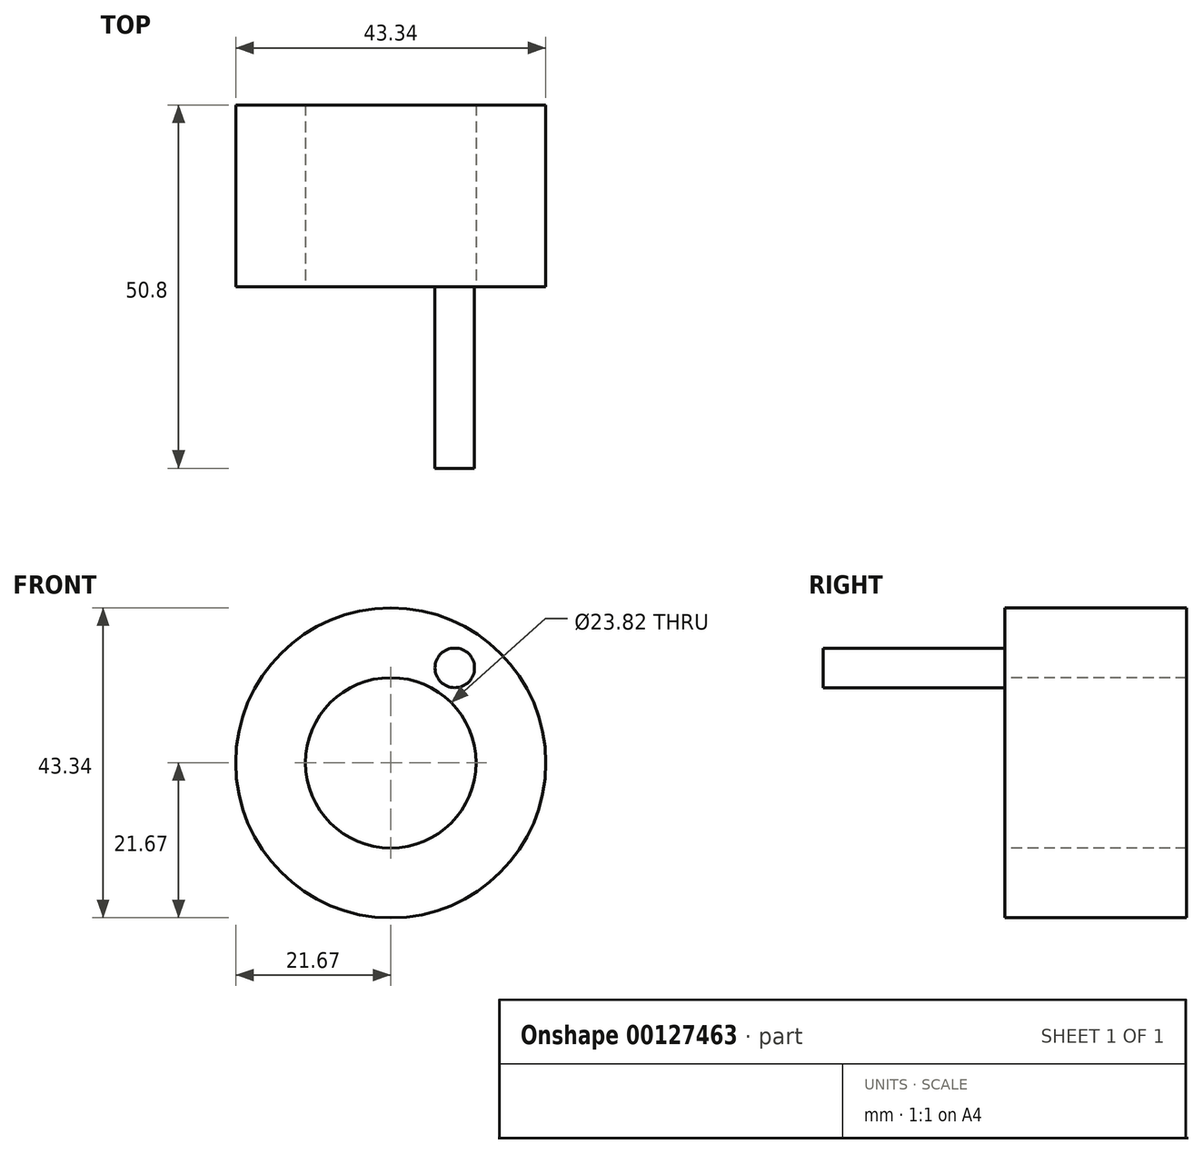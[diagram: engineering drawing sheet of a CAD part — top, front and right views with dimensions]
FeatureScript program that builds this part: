
annotation { "Feature Type Name" : "Feature", "Feature Type Description" : "" }
export const myFeature = defineFeature(function(context is Context, id is Id, definition is map)
    precondition{}
    {
        {
            var Q0;
            Q0=qCreatedBy(makeId("Front.planeOp"),FACE);
            var sketch = newSketch(context, id + "F0", { "sketchPlane" : qUnion([Q0])});
            skCircle(sketch, "E0", {"center": v(0, 0) * mm, "radius": 21.67 * mm});
            skSolve(sketch);
        }
        {
            var Q0;
            Q0=makeQuery(id+"F0.imprint","IMPRINT",FACE,{"disambiguationData":[TD([[makeQuery(id+"F0.imprint","IMPRINT",EDGE,{"derivedFrom":sQuery(id+"F0.wireOp",EDGE,"E0")}),1.0]])]});
            extrude(context, id + "F1", {"entities" : qUnion([Q0]), "oppositeDirection" : true, "depth" : 25.4 * mm});
        }
        {
            var Q0;
            Q0=makeQuery(id+"F1.opExtrude","CAP_FACE",FACE,{"disambiguationData":[OSD([sQuery(id+"F0.wireOp",EDGE,"E0")])],"isStart":true});
            var sketch = newSketch(context, id + "F2", { "sketchPlane" : qUnion([Q0])});
            skCircle(sketch, "E1", {"center": v(0, 0) * mm, "radius": 11.91 * mm});
            skSolve(sketch);
        }
        {
            var Q0;
            Q0=qSketchRegion(id+"F2",true);
            extrude(context, id + "F3", {"entities" : qUnion([Q0]), "operationType" : NewBodyOperationType.REMOVE, "oppositeDirection" : true, "depth" : 58.53 * mm});
        }
        {
            var Q0;
            Q0=makeQuery(id+"F1.opExtrude","CAP_FACE",FACE,{"disambiguationData":[OSD([sQuery(id+"F0.wireOp",EDGE,"E0")])],"isStart":true});
            var sketch = newSketch(context, id + "F4", { "sketchPlane" : qUnion([Q0])});
            skCircle(sketch, "E2", {"center": v(8.95, 13.27) * mm, "radius": 2.77 * mm});
            skSolve(sketch);
        }
        {
            var Q0;
            Q0=qSketchRegion(id+"F4",true);
            extrude(context, id + "F5", {"entities" : qUnion([Q0]), "operationType" : NewBodyOperationType.ADD, "depth" : 25.4 * mm});
        }
    });
